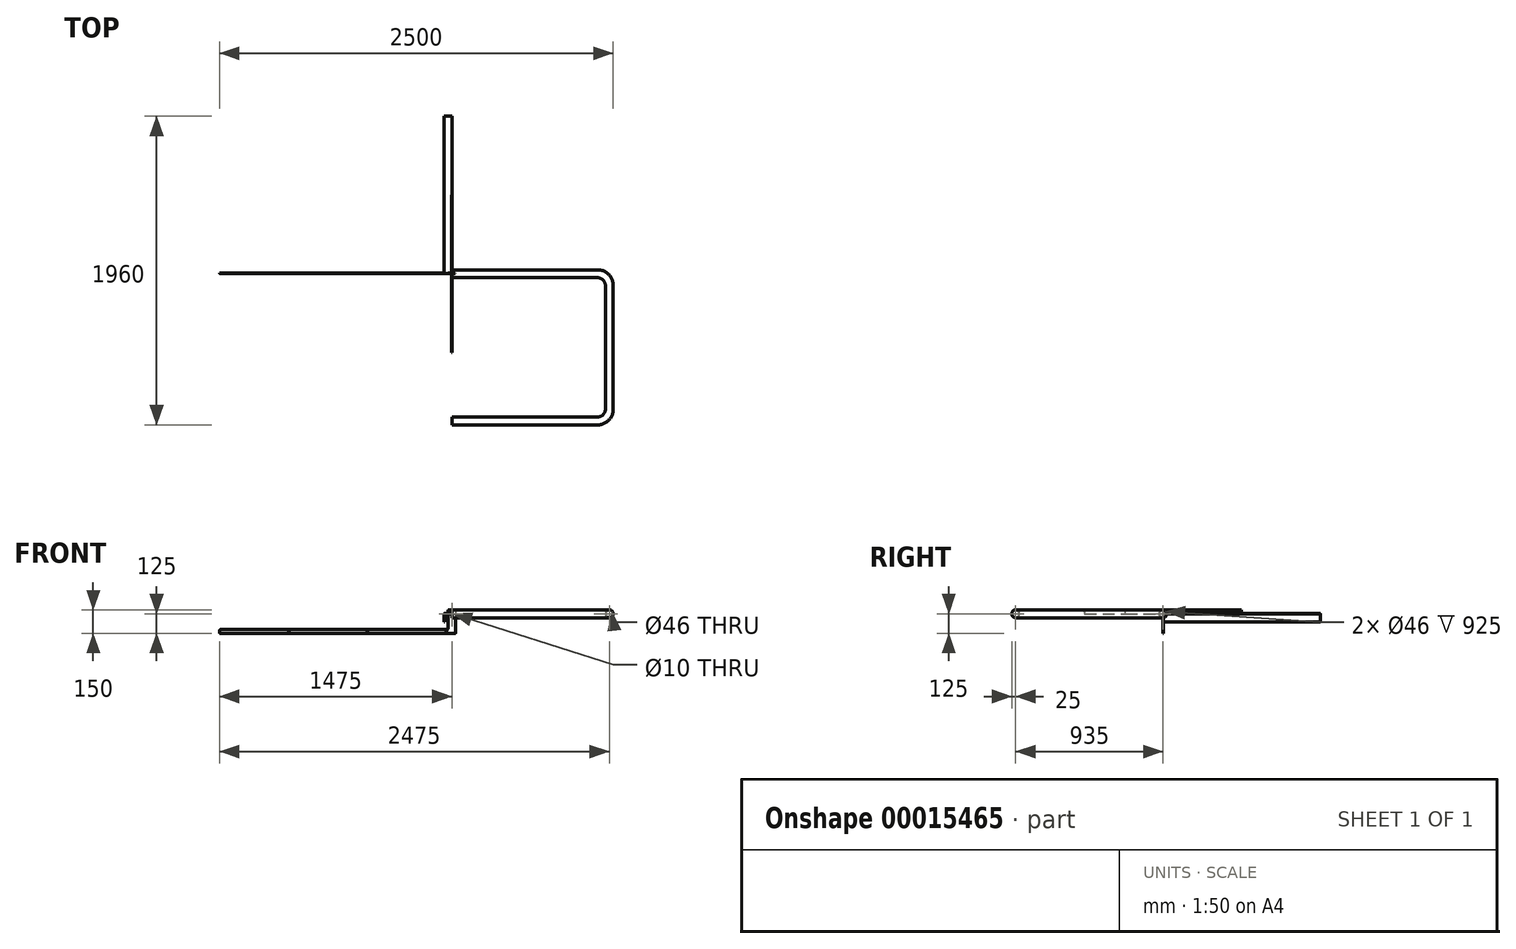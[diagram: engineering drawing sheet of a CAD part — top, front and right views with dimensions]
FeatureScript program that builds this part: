
annotation { "Feature Type Name" : "Feature", "Feature Type Description" : "" }
export const myFeature = defineFeature(function(context is Context, id is Id, definition is map)
    precondition{}
    {
        {
            var Q0;
            Q0=qCreatedBy(makeId("Front.planeOp"),FACE);
            var sketch = newSketch(context, id + "F0", { "sketchPlane" : qUnion([Q0])});
            skLineSegment(sketch, "E0", {"start": v(-1470, -100) * mm, "end": v(-1038, -100) * mm});
            skLineSegment(sketch, "E1", {"start": v(-25, -95) * mm, "end": v(-25, 20) * mm});
            skLineSegment(sketch, "E2", {"start": v(-20, 25) * mm, "end": v(20, 25) * mm});
            skLineSegment(sketch, "E3", {"start": v(25, 20) * mm, "end": v(25, -120) * mm});
            skLineSegment(sketch, "E4", {"start": v(20, -125) * mm, "end": v(-1470, -125) * mm});
            skLineSegment(sketch, "E5", {"start": v(-1475, -105) * mm, "end": v(-1475, -120) * mm});
            skCircle(sketch, "E6", {"center": v(0, 0) * mm, "radius": 5 * mm});
            skPoint(sketch, "E7.visualSharp", {"position": v(-25, 25) * mm});
            skArc(sketch, "E7.filletArc", {"start": v(-20, 25) * mm, "mid": v(-23.54, 23.54) * mm, "end": v(-25, 20) * mm});
            skPoint(sketch, "E8.visualSharp", {"position": v(25, 25) * mm});
            skArc(sketch, "E8.filletArc", {"start": v(25, 20) * mm, "mid": v(23.54, 23.54) * mm, "end": v(20, 25) * mm});
            skPoint(sketch, "E9.visualSharp", {"position": v(-25, -100) * mm});
            skArc(sketch, "E9.filletArc", {"start": v(-30, -100) * mm, "mid": v(-26.46, -98.54) * mm, "end": v(-25, -95) * mm});
            skPoint(sketch, "E10.visualSharp", {"position": v(25, -125) * mm});
            skArc(sketch, "E10.filletArc", {"start": v(20, -125) * mm, "mid": v(23.54, -123.54) * mm, "end": v(25, -120) * mm});
            skPoint(sketch, "E11.visualSharp", {"position": v(-1475, -100) * mm});
            skArc(sketch, "E11.filletArc", {"start": v(-1470, -100) * mm, "mid": v(-1473.54, -101.46) * mm, "end": v(-1475, -105) * mm});
            skPoint(sketch, "E12.visualSharp", {"position": v(-1475, -125) * mm});
            skArc(sketch, "E12.filletArc", {"start": v(-1475, -120) * mm, "mid": v(-1473.54, -123.54) * mm, "end": v(-1470, -125) * mm});
            skLineSegment(sketch, "E13", {"start": v(-1038, -100) * mm, "end": v(-1038, -112.5) * mm});
            skLineSegment(sketch, "E14", {"start": v(-1038, -112.5) * mm, "end": v(-1035, -112.5) * mm});
            skLineSegment(sketch, "E15", {"start": v(-1035, -112.5) * mm, "end": v(-1035, -100) * mm});
            skLineSegment(sketch, "E16", {"start": v(-538, -100) * mm, "end": v(-538, -112.5) * mm});
            skLineSegment(sketch, "E17", {"start": v(-538, -112.5) * mm, "end": v(-535, -112.5) * mm});
            skLineSegment(sketch, "E18", {"start": v(-535, -112.5) * mm, "end": v(-535, -100) * mm});
            skLineSegment(sketch, "E19", {"start": v(-38, -100) * mm, "end": v(-38, -112.5) * mm});
            skLineSegment(sketch, "E20", {"start": v(-38, -112.5) * mm, "end": v(-35, -112.5) * mm});
            skLineSegment(sketch, "E21", {"start": v(-35, -112.5) * mm, "end": v(-35, -100) * mm});
            skLineSegment(sketch, "E22.trimOffspring", {"start": v(-35, -100) * mm, "end": v(-30, -100) * mm});
            skLineSegment(sketch, "E23.trimOffspring", {"start": v(-535, -100) * mm, "end": v(-38, -100) * mm});
            skLineSegment(sketch, "E24.trimOffspring", {"start": v(-1035, -100) * mm, "end": v(-538, -100) * mm});
            skSolve(sketch);
        }
        {
            var Q0;
            Q0=makeQuery(id+"F0.imprint","IMPRINT",FACE,{"disambiguationData":[TD([[makeQuery(id+"F0.imprint","IMPRINT",EDGE,{"derivedFrom":sQuery(id+"F0.wireOp",EDGE,"E0")}),-1.0]])]});
            extrude(context, id + "F1", {"entities" : qUnion([Q0]), "oppositeDirection" : true, "depth" : 3 * mm});
        }
        {
            var Q0;
            Q0=qCreatedBy(makeId("Right.planeOp"),FACE);
            var sketch = newSketch(context, id + "F2", { "sketchPlane" : qUnion([Q0])});
            skLineSegment(sketch, "E25", {"start": v(500, 25) * mm, "end": v(-500, 25) * mm});
            skLineSegment(sketch, "E26", {"start": v(-500, 25) * mm, "end": v(-500, 12.5) * mm});
            skLineSegment(sketch, "E27", {"start": v(-497, 0) * mm, "end": v(-240, 0) * mm});
            skLineSegment(sketch, "E28", {"start": v(500, 12.5) * mm, "end": v(500, 25) * mm});
            skLineSegment(sketch, "E29", {"start": v(500, 12.5) * mm, "end": v(497, 12.5) * mm});
            skLineSegment(sketch, "E30", {"start": v(497, 12.5) * mm, "end": v(497, 0) * mm});
            skLineSegment(sketch, "E31", {"start": v(-500, 12.5) * mm, "end": v(-497, 12.5) * mm});
            skLineSegment(sketch, "E32", {"start": v(-497, 12.5) * mm, "end": v(-497, 0) * mm});
            skLineSegment(sketch, "E33", {"start": v(240, 0) * mm, "end": v(240, 12.5) * mm});
            skLineSegment(sketch, "E34", {"start": v(243, 12.5) * mm, "end": v(240, 12.5) * mm});
            skLineSegment(sketch, "E35", {"start": v(243, 12.5) * mm, "end": v(243, 0) * mm});
            skLineSegment(sketch, "E36", {"start": v(-237, 0) * mm, "end": v(-237, 12.5) * mm});
            skLineSegment(sketch, "E37", {"start": v(-237, 12.5) * mm, "end": v(-240, 12.5) * mm});
            skLineSegment(sketch, "E38", {"start": v(-240, 12.5) * mm, "end": v(-240, 0) * mm});
            skPoint(sketch, "E39.orphan", {"position": v(500, 0) * mm});
            skLineSegment(sketch, "E40.trimOffspring", {"start": v(243, 0) * mm, "end": v(497, 0) * mm});
            skLineSegment(sketch, "E41.trimOffspring", {"start": v(-237, 0) * mm, "end": v(240, 0) * mm});
            skPoint(sketch, "E42.orphan", {"position": v(-500, 0) * mm});
            skPoint(sketch, "E43", {"position": v(0, 0) * mm});
            skSolve(sketch);
        }
        {
            var Q0;
            Q0=makeQuery(id+"F2.imprint","IMPRINT",FACE,{"disambiguationData":[TD([[makeQuery(id+"F2.imprint","IMPRINT",EDGE,{"derivedFrom":sQuery(id+"F2.wireOp",EDGE,"E25")}),1.0]])]});
            extrude(context, id + "F3", {"entities" : qUnion([Q0]), "oppositeDirection" : true, "depth" : 3 * mm});
        }
        {
            var Q0;
            Q0=qCreatedBy(makeId("Top.planeOp"),FACE);
            var sketch = newSketch(context, id + "F4", { "sketchPlane" : qUnion([Q0])});
            skLineSegment(sketch, "E44", {"start": v(0, 0) * mm, "end": v(925, 0) * mm});
            skLineSegment(sketch, "E45", {"start": v(1000, -75) * mm, "end": v(1000, -860) * mm});
            skLineSegment(sketch, "E46", {"start": v(925, -935) * mm, "end": v(0, -935) * mm});
            skPoint(sketch, "E47.visualSharp", {"position": v(1000, 0) * mm});
            skArc(sketch, "E47.filletArc", {"start": v(1000, -75) * mm, "mid": v(978.03, -21.97) * mm, "end": v(925, 0) * mm});
            skPoint(sketch, "E48.visualSharp", {"position": v(1000, -935) * mm});
            skArc(sketch, "E48.filletArc", {"start": v(925, -935) * mm, "mid": v(978.03, -913.03) * mm, "end": v(1000, -860) * mm});
            skSolve(sketch);
        }
        {
            var Q0;
            Q0=qCreatedBy(makeId("Right.planeOp"),FACE);
            var sketch = newSketch(context, id + "F5", { "sketchPlane" : qUnion([Q0])});
            skCircle(sketch, "E49", {"center": v(0, 0) * mm, "radius": 25 * mm});
            skCircle(sketch, "E50", {"center": v(0, 0) * mm, "radius": 23 * mm});
            skSolve(sketch);
        }
        {
            var Q0;
            Q0=makeQuery(id+"F5.imprint","IMPRINT",FACE,{"disambiguationData":[TD([[makeQuery(id+"F5.imprint","IMPRINT",EDGE,{"derivedFrom":sQuery(id+"F5.wireOp",EDGE,"E49")}),1.0]])]});
            var Q1;
            Q1=sQuery(id+"F4.wireOp",EDGE,"E44");
            var Q2;
            Q2=sQuery(id+"F4.wireOp",EDGE,"E47.filletArc");
            var Q3;
            Q3=sQuery(id+"F4.wireOp",EDGE,"E45");
            var Q4;
            Q4=sQuery(id+"F4.wireOp",EDGE,"E48.filletArc");
            var Q5;
            Q5=sQuery(id+"F4.wireOp",EDGE,"E46");
            sweep(context, id + "F6", {"profiles" : qUnion([Q0]), "path" : qUnion([Q1, Q2, Q3, Q4, Q5])});
        }
        {
            var Q0;
            Q0=qCreatedBy(makeId("Front.planeOp"),FACE);
            var sketch = newSketch(context, id + "F7", { "sketchPlane" : qUnion([Q0])});
            skLineSegment(sketch, "E51", {"start": v(0, 0) * mm, "end": v(-42, 0) * mm});
            skLineSegment(sketch, "E52", {"start": v(-47, -5) * mm, "end": v(-47, -50) * mm});
            skLineSegment(sketch, "E53", {"start": v(-47, -50) * mm, "end": v(-50, -50) * mm});
            skLineSegment(sketch, "E54", {"start": v(-50, -50) * mm, "end": v(-50, -2) * mm});
            skLineSegment(sketch, "E55", {"start": v(-45, 3) * mm, "end": v(0, 3) * mm});
            skLineSegment(sketch, "E56", {"start": v(0, 3) * mm, "end": v(0, 0) * mm});
            skPoint(sketch, "E57.visualSharp", {"position": v(-50, 3) * mm});
            skArc(sketch, "E57.filletArc", {"start": v(-45, 3) * mm, "mid": v(-48.54, 1.54) * mm, "end": v(-50, -2) * mm});
            skPoint(sketch, "E58.visualSharp", {"position": v(-47, 0) * mm});
            skArc(sketch, "E58.filletArc", {"start": v(-42, 0) * mm, "mid": v(-45.54, -1.46) * mm, "end": v(-47, -5) * mm});
            skSolve(sketch);
        }
        {
            var Q0;
            Q0=makeQuery(id+"F7.imprint","IMPRINT",FACE,{"disambiguationData":[TD([[makeQuery(id+"F7.imprint","IMPRINT",EDGE,{"derivedFrom":sQuery(id+"F7.wireOp",EDGE,"E51")}),-1.0]])]});
            extrude(context, id + "F8", {"entities" : qUnion([Q0]), "oppositeDirection" : true, "depth" : 1000 * mm});
        }
    });
